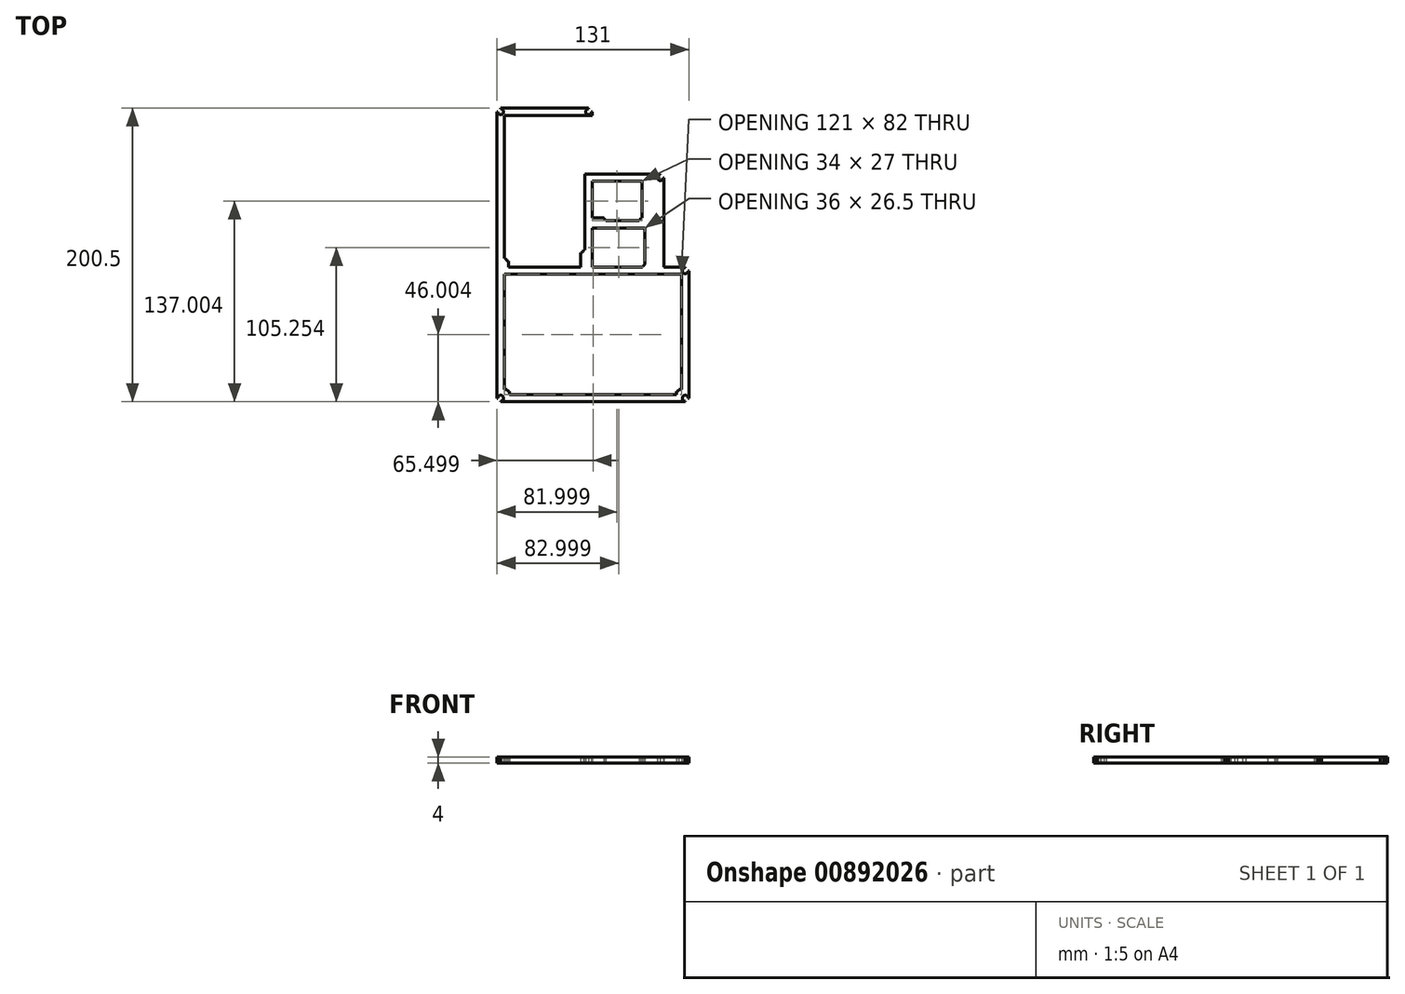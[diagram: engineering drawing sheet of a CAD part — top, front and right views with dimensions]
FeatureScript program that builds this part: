
annotation { "Feature Type Name" : "Feature", "Feature Type Description" : "" }
export const myFeature = defineFeature(function(context is Context, id is Id, definition is map)
    precondition{}
    {
        {
            var Q0;
            Q0=qCreatedBy(makeId("Top.planeOp"),FACE);
            var sketch = newSketch(context, id + "F0", { "sketchPlane" : qUnion([Q0])});
            skLineSegment(sketch, "E0.bottom", {"start": v(-40.7, -58.83) * mm, "end": v(14.3, -58.83) * mm});
            skLineSegment(sketch, "E0.top", {"start": v(-40.7, 44.67) * mm, "end": v(14.3, 44.67) * mm});
            skLineSegment(sketch, "E0.left", {"start": v(-40.7, -58.83) * mm, "end": v(-40.7, 44.67) * mm});
            skLineSegment(sketch, "E0.right", {"start": v(14.3, -58.83) * mm, "end": v(14.3, 44.67) * mm});
            skLineSegment(sketch, "E1.bottom", {"start": v(-45.7, 49.67) * mm, "end": v(85.3, 49.67) * mm});
            skLineSegment(sketch, "E1.top", {"start": v(-45.7, -150.83) * mm, "end": v(85.3, -150.83) * mm});
            skLineSegment(sketch, "E1.left", {"start": v(-45.7, 49.67) * mm, "end": v(-45.7, -150.83) * mm});
            skLineSegment(sketch, "E1.right", {"start": v(85.3, 49.67) * mm, "end": v(85.3, -150.83) * mm});
            skLineSegment(sketch, "E2.bottom", {"start": v(-40.7, -63.83) * mm, "end": v(80.3, -63.83) * mm});
            skLineSegment(sketch, "E2.top", {"start": v(-40.7, -145.83) * mm, "end": v(80.3, -145.83) * mm});
            skLineSegment(sketch, "E2.left", {"start": v(-40.7, -63.83) * mm, "end": v(-40.7, -145.83) * mm});
            skLineSegment(sketch, "E2.right", {"start": v(80.3, -63.83) * mm, "end": v(80.3, -145.83) * mm});
            skLineSegment(sketch, "E3.top", {"start": v(14.3, -63.83) * mm, "end": v(19.3, -63.83) * mm});
            skLineSegment(sketch, "E4.bottom", {"start": v(19.3, -58.83) * mm, "end": v(55.3, -58.83) * mm});
            skLineSegment(sketch, "E4.top", {"start": v(19.3, -32.33) * mm, "end": v(55.3, -32.33) * mm});
            skLineSegment(sketch, "E4.left", {"start": v(19.3, -58.83) * mm, "end": v(19.3, -32.33) * mm});
            skLineSegment(sketch, "E4.right", {"start": v(55.3, -58.83) * mm, "end": v(55.3, -32.33) * mm});
            skLineSegment(sketch, "E5.right", {"start": v(14.3, -32.33) * mm, "end": v(14.3, -27.33) * mm});
            skLineSegment(sketch, "E6.bottom", {"start": v(19.3, -27.33) * mm, "end": v(53.3, -27.33) * mm});
            skLineSegment(sketch, "E6.top", {"start": v(19.3, -0.33) * mm, "end": v(53.3, -0.33) * mm});
            skLineSegment(sketch, "E6.left", {"start": v(19.3, -27.33) * mm, "end": v(19.3, -0.33) * mm});
            skLineSegment(sketch, "E6.right", {"start": v(53.3, -27.33) * mm, "end": v(53.3, -0.33) * mm});
            skLineSegment(sketch, "E7", {"start": v(53.3, -27.33) * mm, "end": v(53.3, -22.33) * mm});
            skLineSegment(sketch, "E8", {"start": v(53.3, -22.33) * mm, "end": v(53.3, -5.33) * mm});
            skLineSegment(sketch, "E9.bottom", {"start": v(53.3, -5.33) * mm, "end": v(53.3, -5.33) * mm});
            skLineSegment(sketch, "E9.top", {"start": v(53.3, -22.33) * mm, "end": v(53.3, -22.33) * mm});
            skLineSegment(sketch, "E9.left", {"start": v(53.3, -5.33) * mm, "end": v(53.3, -22.33) * mm});
            skLineSegment(sketch, "E9.right", {"start": v(53.3, -5.33) * mm, "end": v(53.3, -22.33) * mm});
            skLineSegment(sketch, "E10.bottom", {"start": v(53.3, -22.33) * mm, "end": v(63.3, -22.33) * mm});
            skLineSegment(sketch, "E10.top", {"start": v(53.3, -5.33) * mm, "end": v(63.3, -5.33) * mm});
            skLineSegment(sketch, "E10.right", {"start": v(63.3, -22.33) * mm, "end": v(63.3, -5.33) * mm});
            skLineSegment(sketch, "E11.bottom", {"start": v(14.3, 44.67) * mm, "end": v(19.3, 44.67) * mm});
            skLineSegment(sketch, "E11.top", {"start": v(14.3, 49.67) * mm, "end": v(19.3, 49.67) * mm});
            skLineSegment(sketch, "E11.left", {"start": v(14.3, 44.67) * mm, "end": v(14.3, 49.67) * mm});
            skLineSegment(sketch, "E11.right", {"start": v(19.3, 44.67) * mm, "end": v(19.3, 49.67) * mm});
            skLineSegment(sketch, "E12.bottom", {"start": v(19.3, -0.33) * mm, "end": v(14.3, -0.33) * mm});
            skLineSegment(sketch, "E12.top", {"start": v(19.3, 4.67) * mm, "end": v(14.3, 4.67) * mm});
            skLineSegment(sketch, "E12.left", {"start": v(19.3, -0.33) * mm, "end": v(19.3, 4.67) * mm});
            skLineSegment(sketch, "E12.right", {"start": v(14.3, -0.33) * mm, "end": v(14.3, 4.67) * mm});
            skLineSegment(sketch, "E13.bottom", {"start": v(85.3, 49.67) * mm, "end": v(80.3, 49.67) * mm});
            skLineSegment(sketch, "E13.left", {"start": v(85.3, 49.67) * mm, "end": v(85.3, 44.67) * mm});
            skLineSegment(sketch, "E14.top", {"start": v(19.3, 49.67) * mm, "end": v(85.3, 49.67) * mm});
            skLineSegment(sketch, "E14.left", {"start": v(19.3, 4.67) * mm, "end": v(19.3, 49.67) * mm});
            skLineSegment(sketch, "E14.right", {"start": v(85.3, 4.67) * mm, "end": v(85.3, 49.67) * mm});
            skLineSegment(sketch, "E15.bottom", {"start": v(80.3, -63.83) * mm, "end": v(85.3, -63.83) * mm});
            skLineSegment(sketch, "E15.top", {"start": v(80.3, -58.83) * mm, "end": v(85.3, -58.83) * mm});
            skLineSegment(sketch, "E15.left", {"start": v(80.3, -63.83) * mm, "end": v(80.3, -58.83) * mm});
            skLineSegment(sketch, "E15.right", {"start": v(85.3, -63.83) * mm, "end": v(85.3, -58.83) * mm});
            skLineSegment(sketch, "E16", {"start": v(63.3, -5.33) * mm, "end": v(68.3, -5.33) * mm});
            skLineSegment(sketch, "E17", {"start": v(68.3, -5.33) * mm, "end": v(68.3, -22.33) * mm});
            skLineSegment(sketch, "E18.bottom", {"start": v(85.3, -58.83) * mm, "end": v(68.3, -58.83) * mm});
            skLineSegment(sketch, "E18.left", {"start": v(85.3, -58.83) * mm, "end": v(85.3, 4.67) * mm});
            skLineSegment(sketch, "E18.right", {"start": v(68.3, -58.83) * mm, "end": v(68.3, 4.67) * mm});
            skLineSegment(sketch, "E19", {"start": v(19.3, 4.67) * mm, "end": v(68.3, 4.67) * mm});
            skLineSegment(sketch, "E20.bottom", {"start": v(68.3, 4.67) * mm, "end": v(65.8, 4.67) * mm});
            skLineSegment(sketch, "E20.top", {"start": v(68.3, 2.17) * mm, "end": v(65.8, 2.17) * mm});
            skLineSegment(sketch, "E20.left", {"start": v(68.3, 4.67) * mm, "end": v(68.3, 2.17) * mm});
            skLineSegment(sketch, "E20.right", {"start": v(65.8, 4.67) * mm, "end": v(65.8, 2.17) * mm});
            skLineSegment(sketch, "E21.bottom", {"start": v(19.3, 44.67) * mm, "end": v(16.8, 44.67) * mm});
            skLineSegment(sketch, "E21.top", {"start": v(19.3, 47.17) * mm, "end": v(16.8, 47.17) * mm});
            skLineSegment(sketch, "E21.left", {"start": v(19.3, 44.67) * mm, "end": v(19.3, 47.17) * mm});
            skLineSegment(sketch, "E22.bottom", {"start": v(85.3, -58.83) * mm, "end": v(82.8, -58.83) * mm});
            skLineSegment(sketch, "E22.top", {"start": v(85.3, -61.33) * mm, "end": v(82.8, -61.33) * mm});
            skLineSegment(sketch, "E22.left", {"start": v(85.3, -58.83) * mm, "end": v(85.3, -61.33) * mm});
            skLineSegment(sketch, "E22.right", {"start": v(82.8, -58.83) * mm, "end": v(82.8, -61.33) * mm});
            skLineSegment(sketch, "E23.bottom", {"start": v(85.3, -150.83) * mm, "end": v(82.8, -150.83) * mm});
            skLineSegment(sketch, "E23.top", {"start": v(85.3, -148.33) * mm, "end": v(82.8, -148.33) * mm});
            skLineSegment(sketch, "E23.left", {"start": v(85.3, -150.83) * mm, "end": v(85.3, -148.33) * mm});
            skLineSegment(sketch, "E23.right", {"start": v(82.8, -150.83) * mm, "end": v(82.8, -148.33) * mm});
            skLineSegment(sketch, "E24.bottom", {"start": v(-45.7, -150.83) * mm, "end": v(-43.2, -150.83) * mm});
            skLineSegment(sketch, "E24.top", {"start": v(-45.7, -148.33) * mm, "end": v(-43.2, -148.33) * mm});
            skLineSegment(sketch, "E24.left", {"start": v(-45.7, -150.83) * mm, "end": v(-45.7, -148.33) * mm});
            skLineSegment(sketch, "E24.right", {"start": v(-43.2, -150.83) * mm, "end": v(-43.2, -148.33) * mm});
            skLineSegment(sketch, "E25.bottom", {"start": v(-45.7, 49.67) * mm, "end": v(-43.2, 49.67) * mm});
            skLineSegment(sketch, "E25.top", {"start": v(-45.7, 47.17) * mm, "end": v(-43.2, 47.17) * mm});
            skLineSegment(sketch, "E25.left", {"start": v(-45.7, 49.67) * mm, "end": v(-45.7, 47.17) * mm});
            skLineSegment(sketch, "E25.right", {"start": v(-43.2, 49.67) * mm, "end": v(-43.2, 47.17) * mm});
            skLineSegment(sketch, "E26.bottom", {"start": v(19.3, 49.67) * mm, "end": v(16.8, 49.67) * mm});
            skLineSegment(sketch, "E26.left", {"start": v(19.3, 49.67) * mm, "end": v(19.3, 47.17) * mm});
            skLineSegment(sketch, "E26.right", {"start": v(16.8, 49.67) * mm, "end": v(16.8, 47.17) * mm});
            skCircle(sketch, "E27", {"center": v(16.8, 47.17) * mm, "radius": 2 * mm});
            skCircle(sketch, "E28", {"center": v(65.8, 2.17) * mm, "radius": 2 * mm});
            skCircle(sketch, "E29", {"center": v(82.8, -61.33) * mm, "radius": 2 * mm});
            skCircle(sketch, "E30", {"center": v(82.8, -148.33) * mm, "radius": 2 * mm});
            skCircle(sketch, "E31", {"center": v(-43.2, -148.33) * mm, "radius": 2 * mm});
            skCircle(sketch, "E32", {"center": v(-43.2, 47.17) * mm, "radius": 2 * mm});
            skLineSegment(sketch, "E33.bottom", {"start": v(-40.7, -63.83) * mm, "end": v(-37.3, -63.83) * mm});
            skLineSegment(sketch, "E33.top", {"start": v(-40.7, -67.23) * mm, "end": v(-37.3, -67.23) * mm});
            skLineSegment(sketch, "E33.left", {"start": v(-40.7, -63.83) * mm, "end": v(-40.7, -67.23) * mm});
            skLineSegment(sketch, "E33.right", {"start": v(-37.3, -63.83) * mm, "end": v(-37.3, -67.23) * mm});
            skLineSegment(sketch, "E34.bottom", {"start": v(-40.7, -145.83) * mm, "end": v(-37.3, -145.83) * mm});
            skLineSegment(sketch, "E34.top", {"start": v(-40.7, -142.43) * mm, "end": v(-37.3, -142.43) * mm});
            skLineSegment(sketch, "E34.left", {"start": v(-40.7, -145.83) * mm, "end": v(-40.7, -142.43) * mm});
            skLineSegment(sketch, "E34.right", {"start": v(-37.3, -145.83) * mm, "end": v(-37.3, -142.43) * mm});
            skLineSegment(sketch, "E35.bottom", {"start": v(80.3, -145.83) * mm, "end": v(76.9, -145.83) * mm});
            skLineSegment(sketch, "E35.top", {"start": v(80.3, -142.43) * mm, "end": v(76.9, -142.43) * mm});
            skLineSegment(sketch, "E35.left", {"start": v(80.3, -145.83) * mm, "end": v(80.3, -142.43) * mm});
            skLineSegment(sketch, "E35.right", {"start": v(76.9, -145.83) * mm, "end": v(76.9, -142.43) * mm});
            skLineSegment(sketch, "E36.bottom", {"start": v(80.3, -63.83) * mm, "end": v(76.9, -63.83) * mm});
            skLineSegment(sketch, "E36.top", {"start": v(80.3, -67.23) * mm, "end": v(76.9, -67.23) * mm});
            skLineSegment(sketch, "E36.left", {"start": v(80.3, -63.83) * mm, "end": v(80.3, -67.23) * mm});
            skLineSegment(sketch, "E36.right", {"start": v(76.9, -63.83) * mm, "end": v(76.9, -67.23) * mm});
            skLineSegment(sketch, "E37.bottom", {"start": v(-40.7, -58.83) * mm, "end": v(-37.7, -58.83) * mm});
            skLineSegment(sketch, "E37.top", {"start": v(-40.7, 28.47) * mm, "end": v(-37.7, 28.47) * mm});
            skLineSegment(sketch, "E37.left", {"start": v(-40.7, -58.83) * mm, "end": v(-40.7, 28.47) * mm});
            skLineSegment(sketch, "E37.right", {"start": v(-37.7, -58.83) * mm, "end": v(-37.7, 28.47) * mm});
            skLineSegment(sketch, "E38.bottom", {"start": v(-37.7, -58.83) * mm, "end": v(-40.7, -58.83) * mm});
            skLineSegment(sketch, "E38.top", {"start": v(-37.7, -52.83) * mm, "end": v(-40.7, -52.83) * mm});
            skLineSegment(sketch, "E38.left", {"start": v(-37.7, -58.83) * mm, "end": v(-37.7, -52.83) * mm});
            skLineSegment(sketch, "E38.right", {"start": v(-40.7, -58.83) * mm, "end": v(-40.7, -52.83) * mm});
            skLineSegment(sketch, "E39.bottom", {"start": v(14.3, -58.83) * mm, "end": v(11.3, -58.83) * mm});
            skLineSegment(sketch, "E39.top", {"start": v(14.3, 29.87) * mm, "end": v(11.3, 29.87) * mm});
            skLineSegment(sketch, "E39.left", {"start": v(14.3, -58.83) * mm, "end": v(14.3, 29.87) * mm});
            skLineSegment(sketch, "E39.right", {"start": v(11.3, -58.83) * mm, "end": v(11.3, 29.87) * mm});
            skLineSegment(sketch, "E40.top", {"start": v(14.3, -47.23) * mm, "end": v(11.3, -47.23) * mm});
            skLineSegment(sketch, "E40.left", {"start": v(14.3, -58.83) * mm, "end": v(14.3, -47.23) * mm});
            skLineSegment(sketch, "E40.right", {"start": v(11.3, -58.83) * mm, "end": v(11.3, -47.23) * mm});
            skCircle(sketch, "E41", {"center": v(-37.7, -52.83) * mm, "radius": 2 * mm});
            skCircle(sketch, "E42", {"center": v(-37.7, 28.47) * mm, "radius": 2 * mm});
            skCircle(sketch, "E43", {"center": v(11.3, 29.87) * mm, "radius": 2 * mm});
            skCircle(sketch, "E44", {"center": v(11.3, -47.23) * mm, "radius": 2 * mm});
            skLineSegment(sketch, "E45.bottom", {"start": v(19.3, -0.33) * mm, "end": v(28.55, -0.33) * mm});
            skLineSegment(sketch, "E45.top", {"start": v(19.3, -2.28) * mm, "end": v(28.55, -2.28) * mm});
            skLineSegment(sketch, "E45.left", {"start": v(19.3, -0.33) * mm, "end": v(19.3, -2.28) * mm});
            skLineSegment(sketch, "E45.right", {"start": v(28.55, -0.33) * mm, "end": v(28.55, -2.28) * mm});
            skLineSegment(sketch, "E46.bottom", {"start": v(19.3, -27.33) * mm, "end": v(28.55, -27.33) * mm});
            skLineSegment(sketch, "E46.top", {"start": v(19.3, -25.38) * mm, "end": v(28.55, -25.38) * mm});
            skLineSegment(sketch, "E46.left", {"start": v(19.3, -27.33) * mm, "end": v(19.3, -25.38) * mm});
            skLineSegment(sketch, "E46.right", {"start": v(28.55, -27.33) * mm, "end": v(28.55, -25.38) * mm});
            skLineSegment(sketch, "E47.bottom", {"start": v(53.3, -0.33) * mm, "end": v(51.35, -0.33) * mm});
            skLineSegment(sketch, "E47.top", {"start": v(53.3, -2.28) * mm, "end": v(51.35, -2.28) * mm});
            skLineSegment(sketch, "E47.left", {"start": v(53.3, -0.33) * mm, "end": v(53.3, -2.28) * mm});
            skLineSegment(sketch, "E47.right", {"start": v(51.35, -0.33) * mm, "end": v(51.35, -2.28) * mm});
            skLineSegment(sketch, "E48.bottom", {"start": v(53.3, -27.33) * mm, "end": v(51.35, -27.33) * mm});
            skLineSegment(sketch, "E48.top", {"start": v(53.3, -25.38) * mm, "end": v(51.35, -25.38) * mm});
            skLineSegment(sketch, "E48.left", {"start": v(53.3, -27.33) * mm, "end": v(53.3, -25.38) * mm});
            skLineSegment(sketch, "E48.right", {"start": v(51.35, -27.33) * mm, "end": v(51.35, -25.38) * mm});
            skLineSegment(sketch, "E49.bottom", {"start": v(55.3, -32.33) * mm, "end": v(53.6, -32.33) * mm});
            skLineSegment(sketch, "E49.top", {"start": v(55.3, -34.03) * mm, "end": v(53.6, -34.03) * mm});
            skLineSegment(sketch, "E49.left", {"start": v(55.3, -32.33) * mm, "end": v(55.3, -34.03) * mm});
            skLineSegment(sketch, "E49.right", {"start": v(53.6, -32.33) * mm, "end": v(53.6, -34.03) * mm});
            skLineSegment(sketch, "E50.bottom", {"start": v(55.3, -58.83) * mm, "end": v(53.6, -58.83) * mm});
            skLineSegment(sketch, "E50.top", {"start": v(55.3, -57.13) * mm, "end": v(53.6, -57.13) * mm});
            skLineSegment(sketch, "E50.left", {"start": v(55.3, -58.83) * mm, "end": v(55.3, -57.13) * mm});
            skLineSegment(sketch, "E50.right", {"start": v(53.6, -58.83) * mm, "end": v(53.6, -57.13) * mm});
            skCircle(sketch, "E51", {"center": v(53.6, -34.03) * mm, "radius": 1.2 * mm});
            skCircle(sketch, "E52", {"center": v(53.6, -57.13) * mm, "radius": 1.2 * mm});
            skCircle(sketch, "E53", {"center": v(51.35, -25.38) * mm, "radius": 1.15 * mm});
            skCircle(sketch, "E54", {"center": v(28.55, -25.38) * mm, "radius": 1.15 * mm});
            skCircle(sketch, "E55", {"center": v(28.55, -2.28) * mm, "radius": 1.15 * mm});
            skCircle(sketch, "E56", {"center": v(51.35, -2.28) * mm, "radius": 1.15 * mm});
            skCircle(sketch, "E57", {"center": v(-37.3, -67.23) * mm, "radius": 1.4 * mm});
            skCircle(sketch, "E58", {"center": v(76.9, -67.23) * mm, "radius": 1.4 * mm});
            skCircle(sketch, "E59", {"center": v(-37.3, -142.43) * mm, "radius": 1.4 * mm});
            skCircle(sketch, "E60", {"center": v(76.9, -142.43) * mm, "radius": 1.4 * mm});
            skSolve(sketch);
        }
        {
            var Q0;
            {var subQ1=sQuery(id+"F0.wireOp",EDGE,"E23.bottom");Q0=makeQuery(id+"F0.imprint","IMPRINT",FACE,{"disambiguationData":[TD([[makeQuery(id+"F0.imprint","IMPRINT",EDGE,{"derivedFrom":subQ1}),-1.0]])]});}
            var Q1;
            {var subQ1=sQuery(id+"F0.wireOp",EDGE,"E24.bottom");Q1=makeQuery(id+"F0.imprint","IMPRINT",FACE,{"disambiguationData":[TD([[makeQuery(id+"F0.imprint","IMPRINT",EDGE,{"derivedFrom":subQ1}),1.0]])]});}
            var Q2;
            {var subQ1=sQuery(id+"F0.wireOp",EDGE,"E25.bottom");Q2=makeQuery(id+"F0.imprint","IMPRINT",FACE,{"disambiguationData":[TD([[makeQuery(id+"F0.imprint","IMPRINT",EDGE,{"derivedFrom":subQ1}),-1.0]])]});}
            var Q3;
            {var subQ1=sQuery(id+"F0.wireOp",EDGE,"E22.bottom");Q3=makeQuery(id+"F0.imprint","IMPRINT",FACE,{"disambiguationData":[TD([[makeQuery(id+"F0.imprint","IMPRINT",EDGE,{"derivedFrom":subQ1}),1.0]])]});}
            var Q4;
            {var subQ1=sQuery(id+"F0.wireOp",EDGE,"E26.bottom");Q4=makeQuery(id+"F0.imprint","IMPRINT",FACE,{"disambiguationData":[TD([[makeQuery(id+"F0.imprint","IMPRINT",EDGE,{"derivedFrom":subQ1}),1.0]])]});}
            var Q5;
            Q5=makeQuery(id+"F0.imprint","IMPRINT",FACE,{"disambiguationData":[TD([[makeQuery(id+"F0.imprint","IMPRINT",EDGE,{"derivedFrom":sQuery(id+"F0.wireOp",EDGE,"E15.bottom")}),1.0]])]});
            var Q6;
            Q6=makeQuery(id+"F0.imprint","IMPRINT",FACE,{"disambiguationData":[TD([[makeQuery(id+"F0.imprint","IMPRINT",EDGE,{"derivedFrom":sQuery(id+"F0.wireOp",EDGE,"E11.bottom")}),1.0]])]});
            var Q7;
            {var subQ0=sQuery(id+"F0.wireOp",EDGE,"E12.bottom");Q7=makeQuery(id+"F0.imprint","IMPRINT",FACE,{"disambiguationData":[TD([[makeQuery(id+"F0.imprint","IMPRINT",EDGE,{"derivedFrom":subQ0}),-1.0]])]});}
            var Q8;
            {var subQ1=sQuery(id+"F0.wireOp",EDGE,"E0.right");Q8=makeQuery(id+"F0.imprint","IMPRINT",FACE,{"disambiguationData":[TD([[makeQuery(id+"F0.imprint","IMPRINT",EDGE,{"derivedFrom":subQ1}),-1.0]])]});}
            var Q9;
            Q9=makeQuery(id+"F0.imprint","IMPRINT",FACE,{"disambiguationData":[TD([[makeQuery(id+"F0.imprint","IMPRINT",EDGE,{"derivedFrom":sQuery(id+"F0.wireOp",EDGE,"E6.top")}),1.0]])]});
            var Q10;
            {var subQ1=sQuery(id+"F0.wireOp",EDGE,"E20.bottom");Q10=makeQuery(id+"F0.imprint","IMPRINT",FACE,{"disambiguationData":[TD([[makeQuery(id+"F0.imprint","IMPRINT",EDGE,{"derivedFrom":subQ1}),1.0]])]});}
            var Q11;
            {var subQ7=sQuery(id+"F0.wireOp",EDGE,"E0.bottom");Q11=makeQuery(id+"F0.imprint","IMPRINT",FACE,{"disambiguationData":[TD([[makeQuery(id+"F0.imprint","IMPRINT",EDGE,{"derivedFrom":subQ7}),1.0]])]});}
            var Q12;
            {var subQ1=sQuery(id+"F0.wireOp",EDGE,"E37.left");Q12=makeQuery(id+"F0.imprint","IMPRINT",FACE,{"disambiguationData":[TD([[makeQuery(id+"F0.imprint","IMPRINT",EDGE,{"derivedFrom":subQ1}),-1.0]])]});}
            var Q13;
            {var subQ1=sQuery(id+"F0.wireOp",EDGE,"E38.bottom");Q13=makeQuery(id+"F0.imprint","IMPRINT",FACE,{"disambiguationData":[TD([[makeQuery(id+"F0.imprint","IMPRINT",EDGE,{"derivedFrom":subQ1}),-1.0]])]});}
            var Q14;
            {var subQ1=sQuery(id+"F0.wireOp",EDGE,"E39.bottom");Q14=makeQuery(id+"F0.imprint","IMPRINT",FACE,{"disambiguationData":[TD([[makeQuery(id+"F0.imprint","IMPRINT",EDGE,{"derivedFrom":subQ1}),-1.0]])]});}
            var Q15;
            {var subQ0=sQuery(id+"F0.wireOp",EDGE,"E39.left");var subQ3=makeQuery(id+"F0.imprint","IMPRINT",VERTEX,{"disambiguationData":[OD(0.0)],"derivedFrom":subQ0});Q15=makeQuery(id+"F0.imprint","IMPRINT",FACE,{"disambiguationData":[TD([[makeQuery(id+"F0.imprint","IMPRINT",EDGE,{"disambiguationData":[TD([[subQ3,-1.0]])],"derivedFrom":subQ0}),1.0]])]});}
            var Q16;
            Q16=makeQuery(id+"F0.imprint","IMPRINT",FACE,{"disambiguationData":[TD([[makeQuery(id+"F0.imprint","IMPRINT",EDGE,{"derivedFrom":sQuery(id+"F0.wireOp",EDGE,"E10.bottom")}),1.0]])]});
            var Q17;
            {var subQ1=sQuery(id+"F0.wireOp",EDGE,"E45.bottom");Q17=makeQuery(id+"F0.imprint","IMPRINT",FACE,{"disambiguationData":[TD([[makeQuery(id+"F0.imprint","IMPRINT",EDGE,{"derivedFrom":subQ1}),-1.0]])]});}
            var Q18;
            {var subQ1=sQuery(id+"F0.wireOp",EDGE,"E46.bottom");Q18=makeQuery(id+"F0.imprint","IMPRINT",FACE,{"disambiguationData":[TD([[makeQuery(id+"F0.imprint","IMPRINT",EDGE,{"derivedFrom":subQ1}),1.0]])]});}
            var Q19;
            {var subQ1=sQuery(id+"F0.wireOp",EDGE,"E48.bottom");Q19=makeQuery(id+"F0.imprint","IMPRINT",FACE,{"disambiguationData":[TD([[makeQuery(id+"F0.imprint","IMPRINT",EDGE,{"derivedFrom":subQ1}),-1.0]])]});}
            var Q20;
            {var subQ1=sQuery(id+"F0.wireOp",EDGE,"E47.bottom");Q20=makeQuery(id+"F0.imprint","IMPRINT",FACE,{"disambiguationData":[TD([[makeQuery(id+"F0.imprint","IMPRINT",EDGE,{"derivedFrom":subQ1}),1.0]])]});}
            var Q21;
            {var subQ2=sQuery(id+"F0.wireOp",EDGE,"E4.bottom");Q21=makeQuery(id+"F0.imprint","IMPRINT",FACE,{"disambiguationData":[TD([[makeQuery(id+"F0.imprint","IMPRINT",EDGE,{"derivedFrom":subQ2}),1.0]])]});}
            var Q22;
            {var subQ1=sQuery(id+"F0.wireOp",EDGE,"E49.bottom");Q22=makeQuery(id+"F0.imprint","IMPRINT",FACE,{"disambiguationData":[TD([[makeQuery(id+"F0.imprint","IMPRINT",EDGE,{"derivedFrom":subQ1}),1.0]])]});}
            var Q23;
            {var subQ1=sQuery(id+"F0.wireOp",EDGE,"E50.bottom");Q23=makeQuery(id+"F0.imprint","IMPRINT",FACE,{"disambiguationData":[TD([[makeQuery(id+"F0.imprint","IMPRINT",EDGE,{"derivedFrom":subQ1}),-1.0]])]});}
            var Q24;
            Q24=makeQuery(id+"F0.imprint","IMPRINT",FACE,{"disambiguationData":[TD([[makeQuery(id+"F0.imprint","IMPRINT",EDGE,{"derivedFrom":sQuery(id+"F0.wireOp",EDGE,"E0.bottom")}),-1.0]])]});
            var Q25;
            {var subQ14=sQuery(id+"F0.wireOp",EDGE,"E2.top");Q25=makeQuery(id+"F0.imprint","IMPRINT",FACE,{"disambiguationData":[TD([[makeQuery(id+"F0.imprint","IMPRINT",EDGE,{"derivedFrom":subQ14}),1.0]])]});}
            var Q26;
            {var subQ1=sQuery(id+"F0.wireOp",EDGE,"E33.bottom");Q26=makeQuery(id+"F0.imprint","IMPRINT",FACE,{"disambiguationData":[TD([[makeQuery(id+"F0.imprint","IMPRINT",EDGE,{"derivedFrom":subQ1}),-1.0]])]});}
            var Q27;
            {var subQ1=sQuery(id+"F0.wireOp",EDGE,"E34.bottom");Q27=makeQuery(id+"F0.imprint","IMPRINT",FACE,{"disambiguationData":[TD([[makeQuery(id+"F0.imprint","IMPRINT",EDGE,{"derivedFrom":subQ1}),1.0]])]});}
            var Q28;
            {var subQ1=sQuery(id+"F0.wireOp",EDGE,"E35.bottom");Q28=makeQuery(id+"F0.imprint","IMPRINT",FACE,{"disambiguationData":[TD([[makeQuery(id+"F0.imprint","IMPRINT",EDGE,{"derivedFrom":subQ1}),-1.0]])]});}
            var Q29;
            {var subQ1=sQuery(id+"F0.wireOp",EDGE,"E36.bottom");Q29=makeQuery(id+"F0.imprint","IMPRINT",FACE,{"disambiguationData":[TD([[makeQuery(id+"F0.imprint","IMPRINT",EDGE,{"derivedFrom":subQ1}),1.0]])]});}
            var Q30;
            {var subQ1=sQuery(id+"F0.wireOp",EDGE,"E6.bottom");Q30=makeQuery(id+"F0.imprint","IMPRINT",FACE,{"disambiguationData":[TD([[makeQuery(id+"F0.imprint","IMPRINT",EDGE,{"derivedFrom":subQ1}),1.0]])]});}
            extrude(context, id + "F1", {"entities" : qUnion([Q0, Q1, Q2, Q3, Q4, Q5, Q6, Q7, Q8, Q9, Q10, Q11, Q12, Q13, Q14, Q15, Q16, Q17, Q18, Q19, Q20, Q21, Q22, Q23, Q24, Q25, Q26, Q27, Q28, Q29, Q30]), "depth" : 4 * mm, "offsetDistance" : 25 * mm});
        }
    });
